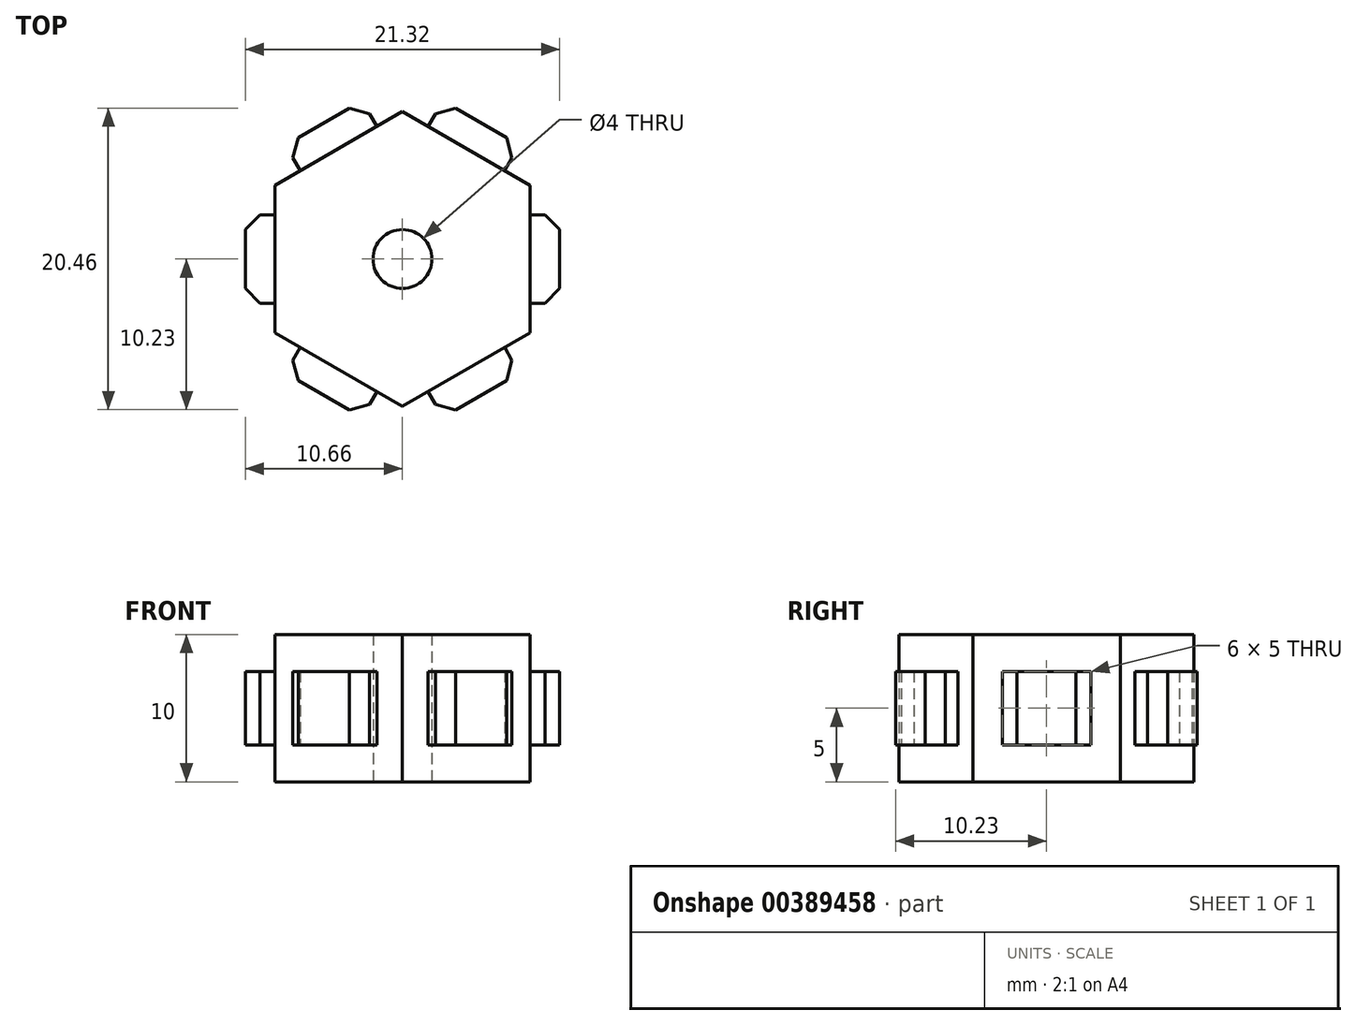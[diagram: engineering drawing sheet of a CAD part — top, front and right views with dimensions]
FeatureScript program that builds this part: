
annotation { "Feature Type Name" : "Feature", "Feature Type Description" : "" }
export const myFeature = defineFeature(function(context is Context, id is Id, definition is map)
    precondition{}
    {
        {
            var Q0;
            Q0=qCreatedBy(makeId("Top.planeOp"),FACE);
            var sketch = newSketch(context, id + "F0", { "sketchPlane" : qUnion([Q0])});
            skCircle(sketch, "E0.cCircle", {"center": v(0, 0) * mm, "radius": 10 * mm, "construction": true});
            skLineSegment(sketch, "E0.0", {"start": v(0, 10) * mm, "end": v(8.66, 5) * mm});
            skLineSegment(sketch, "E0.1", {"start": v(8.66, 5) * mm, "end": v(8.66, -5) * mm});
            skLineSegment(sketch, "E0.2", {"start": v(8.66, -5) * mm, "end": v(0, -10) * mm});
            skLineSegment(sketch, "E0.3", {"start": v(0, -10) * mm, "end": v(-8.66, -5) * mm});
            skLineSegment(sketch, "E0.4", {"start": v(-8.66, -5) * mm, "end": v(-8.66, 5) * mm});
            skLineSegment(sketch, "E0.5", {"start": v(-8.66, 5) * mm, "end": v(0, 10) * mm});
            skCircle(sketch, "E1", {"center": v(0, 0) * mm, "radius": 2 * mm});
            skSolve(sketch);
        }
        {
            var Q0;
            Q0=qSketchRegion(id+"F0",true);
            extrude(context, id + "F1", {"entities" : qUnion([Q0]), "endBound" : BoundingType.SYMMETRIC, "depth" : 10 * mm});
        }
        {
            var Q0;
            Q0=qCreatedBy(makeId("Top.planeOp"),FACE);
            var sketch = newSketch(context, id + "F2", { "sketchPlane" : qUnion([Q0])});
            skLineSegment(sketch, "E2", {"start": v(10.66, 0) * mm, "end": v(10.66, -3) * mm});
            skLineSegment(sketch, "E3", {"start": v(10.66, 0) * mm, "end": v(10.66, 3) * mm});
            skLineSegment(sketch, "E4", {"start": v(8.66, -3) * mm, "end": v(10.66, -3) * mm});
            skLineSegment(sketch, "E5", {"start": v(10.66, 3) * mm, "end": v(8.66, 3) * mm});
            skLineSegment(sketch, "E6", {"start": v(8.66, 0) * mm, "end": v(8.66, 3) * mm});
            skLineSegment(sketch, "E7", {"start": v(8.66, 0) * mm, "end": v(8.66, -3) * mm});
            skLineSegment(sketch, "E8.1.0", {"start": v(5.33, 9.23) * mm, "end": v(2.73, 10.73) * mm});
            skLineSegment(sketch, "E8.1.1", {"start": v(5.33, 9.23) * mm, "end": v(7.93, 7.73) * mm});
            skLineSegment(sketch, "E8.1.2", {"start": v(6.93, 6) * mm, "end": v(7.93, 7.73) * mm});
            skLineSegment(sketch, "E8.1.3", {"start": v(4.33, 7.5) * mm, "end": v(6.93, 6) * mm});
            skLineSegment(sketch, "E8.1.4", {"start": v(4.33, 7.5) * mm, "end": v(1.73, 9) * mm});
            skLineSegment(sketch, "E8.1.5", {"start": v(2.73, 10.73) * mm, "end": v(1.73, 9) * mm});
            skLineSegment(sketch, "E8.2.0", {"start": v(-5.33, 9.23) * mm, "end": v(-7.93, 7.73) * mm});
            skLineSegment(sketch, "E8.2.1", {"start": v(-5.33, 9.23) * mm, "end": v(-2.73, 10.73) * mm});
            skLineSegment(sketch, "E8.2.2", {"start": v(-1.73, 9) * mm, "end": v(-2.73, 10.73) * mm});
            skLineSegment(sketch, "E8.2.3", {"start": v(-4.33, 7.5) * mm, "end": v(-1.73, 9) * mm});
            skLineSegment(sketch, "E8.2.4", {"start": v(-4.33, 7.5) * mm, "end": v(-6.93, 6) * mm});
            skLineSegment(sketch, "E8.2.5", {"start": v(-7.93, 7.73) * mm, "end": v(-6.93, 6) * mm});
            skLineSegment(sketch, "E8.3.0", {"start": v(-10.66, 0) * mm, "end": v(-10.66, -3) * mm});
            skLineSegment(sketch, "E8.3.1", {"start": v(-10.66, 0) * mm, "end": v(-10.66, 3) * mm});
            skLineSegment(sketch, "E8.3.2", {"start": v(-8.66, 3) * mm, "end": v(-10.66, 3) * mm});
            skLineSegment(sketch, "E8.3.3", {"start": v(-8.66, 0) * mm, "end": v(-8.66, 3) * mm});
            skLineSegment(sketch, "E8.3.4", {"start": v(-8.66, 0) * mm, "end": v(-8.66, -3) * mm});
            skLineSegment(sketch, "E8.3.5", {"start": v(-10.66, -3) * mm, "end": v(-8.66, -3) * mm});
            skLineSegment(sketch, "E8.4.0", {"start": v(-5.33, -9.23) * mm, "end": v(-2.73, -10.73) * mm});
            skLineSegment(sketch, "E8.4.1", {"start": v(-5.33, -9.23) * mm, "end": v(-7.93, -7.73) * mm});
            skLineSegment(sketch, "E8.4.2", {"start": v(-6.93, -6) * mm, "end": v(-7.93, -7.73) * mm});
            skLineSegment(sketch, "E8.4.3", {"start": v(-4.33, -7.5) * mm, "end": v(-6.93, -6) * mm});
            skLineSegment(sketch, "E8.4.4", {"start": v(-4.33, -7.5) * mm, "end": v(-1.73, -9) * mm});
            skLineSegment(sketch, "E8.4.5", {"start": v(-2.73, -10.73) * mm, "end": v(-1.73, -9) * mm});
            skLineSegment(sketch, "E8.5.0", {"start": v(5.33, -9.23) * mm, "end": v(7.93, -7.73) * mm});
            skLineSegment(sketch, "E8.5.1", {"start": v(5.33, -9.23) * mm, "end": v(2.73, -10.73) * mm});
            skLineSegment(sketch, "E8.5.2", {"start": v(1.73, -9) * mm, "end": v(2.73, -10.73) * mm});
            skLineSegment(sketch, "E8.5.3", {"start": v(4.33, -7.5) * mm, "end": v(1.73, -9) * mm});
            skLineSegment(sketch, "E8.5.4", {"start": v(4.33, -7.5) * mm, "end": v(6.93, -6) * mm});
            skLineSegment(sketch, "E8.5.5", {"start": v(7.93, -7.73) * mm, "end": v(6.93, -6) * mm});
            skPoint(sketch, "E8.center", {"position": v(0, 0) * mm});
            skSolve(sketch);
        }
        {
            var Q0;
            Q0=qSketchRegion(id+"F2",true);
            extrude(context, id + "F3", {"entities" : qUnion([Q0]), "operationType" : NewBodyOperationType.ADD, "endBound" : BoundingType.SYMMETRIC, "depth" : 5 * mm});
        }
        {
            var Q0;
            Q0=makeQuery(id+"F3.opExtrude","SWEPT_EDGE",EDGE,{"disambiguationData":[OSD([sQuery(id+"F2.wireOp",EDGE,"E3"),sQuery(id+"F2.wireOp",EDGE,"E5")])]});
            var Q1;
            Q1=makeQuery(id+"F3.opExtrude","SWEPT_EDGE",EDGE,{"disambiguationData":[OSD([sQuery(id+"F2.wireOp",EDGE,"E2"),sQuery(id+"F2.wireOp",EDGE,"E4")])]});
            var Q2;
            Q2=makeQuery(id+"F3.opExtrude","SWEPT_EDGE",EDGE,{"disambiguationData":[OSD([sQuery(id+"F2.wireOp",EDGE,"E8.5.0"),sQuery(id+"F2.wireOp",EDGE,"E8.5.5")])]});
            var Q3;
            Q3=makeQuery(id+"F3.opExtrude","SWEPT_EDGE",EDGE,{"disambiguationData":[OSD([sQuery(id+"F2.wireOp",EDGE,"E8.5.1"),sQuery(id+"F2.wireOp",EDGE,"E8.5.2")])]});
            var Q4;
            Q4=makeQuery(id+"F3.opExtrude","SWEPT_EDGE",EDGE,{"disambiguationData":[OSD([sQuery(id+"F2.wireOp",EDGE,"E8.4.0"),sQuery(id+"F2.wireOp",EDGE,"E8.4.5")])]});
            var Q5;
            Q5=makeQuery(id+"F3.opExtrude","SWEPT_EDGE",EDGE,{"disambiguationData":[OSD([sQuery(id+"F2.wireOp",EDGE,"E8.4.1"),sQuery(id+"F2.wireOp",EDGE,"E8.4.2")])]});
            var Q6;
            Q6=makeQuery(id+"F3.opExtrude","SWEPT_EDGE",EDGE,{"disambiguationData":[OSD([sQuery(id+"F2.wireOp",EDGE,"E8.3.0"),sQuery(id+"F2.wireOp",EDGE,"E8.3.5")])]});
            var Q7;
            Q7=makeQuery(id+"F3.opExtrude","SWEPT_EDGE",EDGE,{"disambiguationData":[OSD([sQuery(id+"F2.wireOp",EDGE,"E8.3.1"),sQuery(id+"F2.wireOp",EDGE,"E8.3.2")])]});
            var Q8;
            Q8=makeQuery(id+"F3.opExtrude","SWEPT_EDGE",EDGE,{"disambiguationData":[OSD([sQuery(id+"F2.wireOp",EDGE,"E8.2.0"),sQuery(id+"F2.wireOp",EDGE,"E8.2.5")])]});
            var Q9;
            Q9=makeQuery(id+"F3.opExtrude","SWEPT_EDGE",EDGE,{"disambiguationData":[OSD([sQuery(id+"F2.wireOp",EDGE,"E8.2.1"),sQuery(id+"F2.wireOp",EDGE,"E8.2.2")])]});
            var Q10;
            Q10=makeQuery(id+"F3.opExtrude","SWEPT_EDGE",EDGE,{"disambiguationData":[OSD([sQuery(id+"F2.wireOp",EDGE,"E8.1.0"),sQuery(id+"F2.wireOp",EDGE,"E8.1.5")])]});
            var Q11;
            Q11=makeQuery(id+"F3.opExtrude","SWEPT_EDGE",EDGE,{"disambiguationData":[OSD([sQuery(id+"F2.wireOp",EDGE,"E8.1.1"),sQuery(id+"F2.wireOp",EDGE,"E8.1.2")])]});
            chamfer(context, id + "F4", {"entities" : qUnion([Q0, Q1, Q2, Q3, Q4, Q5, Q6, Q7, Q8, Q9, Q10, Q11]), "width" : 1 * mm, "tangentPropagation" : true});
        }
    });
